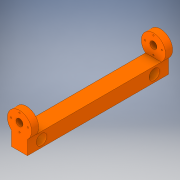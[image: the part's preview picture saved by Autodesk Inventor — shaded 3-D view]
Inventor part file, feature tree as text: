
AUTODESK INVENTOR PART (.ipt)
format: ipt  version: 2019 (Build 230136000, 136)  size: 166,400 bytes
history: native  units: in
note: dims shown in document units (in); Inventor stores cm internally (conversion verified against a paired STEP export)
features: extrude x3, sketch x3, plane x1, mirror x1
ambient origin geometry x8: Origin, YZ Plane, XZ Plane, XY Plane, X Axis, Y Axis, Z Axis, Center Point
bodies: Solid1 (feature_tree)
feature tree (8):
  extrude  "Extrusion1"  Depth=0.565in
  extrude  "Extrusion2"  Depth=0.5in
  sketch  "Sketch3"  dims[d5=0.375in d6=4.0in d7=5.0in d8=0.5in d9=0.5in d10=0.25in d11=0.25in d12=0.5in d13=0.0in d15=0.75in d16=0.0469in d17=0.0469in d18=0.0469in d19=0.0469in d20=0.3in d28=0.0in d29=0.43in d32=0.25in d33=0.3in d34=0.3in d35=0.3in d36=0.0in d37=0.3792in d38=0.0in d39=0.0in d40=0.0in d41=0.25in d42=0.0in]
  plane  "Work Plane1"
  extrude  "Extrusion4"  Depth=0.25in
  mirror  "Mirror1"
  sketch  "Sketch1"  dims[d0=5.0in d1=0.565in]
  sketch  "Sketch2"  dims[d2=0.5in d3=0.0in d4=0.375in]
